# Revit family: K-Series Bar Joist-Rod Web
name_source: partatom
category: Structural Framing
revit_build: Autodesk Revit Architecture 2012 (Build: 20110210_1515)
units: mm (PartAtom-declared; Revit-internal decimal feet)

## types (64) — shared parameters
Assembly Code = B1010350
Chord Thickness = 0' - 0 1/4"
Cord Leg = 0' - 1 1/4"
Rendering Material = <By Category>
Seat Depth = 0' - 2 1/2"
Seat Length = 0' - 4"
Web Thickness = 0' - 0 3/8"

## per-type parameters (varying)
| type | Depth | End Panel | Wt |
| 8K1 | 0' - 8" | 1' - 4" | 5 |
| 10K1 | 0' - 10" | 1' - 8" | 5 |
| 12K1 | 1' - 0" | 2' - 0" | 5 |
| 12K3 | 1' - 0" | 2' - 0" | 6 |
| 12K5 | 1' - 0" | 2' - 0" | 7 |
| 14K1 | 1' - 2" | 2' - 4" | 5 |
| 14K3 | 1' - 2" | 2' - 4" | 6 |
| 14K4 | 1' - 2" | 2' - 4" | 7 |
| 14K6 | 1' - 2" | 2' - 4" | 8 |
| 16K2 | 1' - 4" | 2' - 8" | 6 |
| 16K3 | 1' - 4" | 2' - 8" | 6 |
| 16K4 | 1' - 4" | 2' - 8" | 7 |
| 16K5 | 1' - 4" | 2' - 8" | 8 |
| 16K6 | 1' - 4" | 2' - 8" | 8 |
| 16K7 | 1' - 4" | 2' - 8" | 9 |
| 16K9 | 1' - 4" | 2' - 8" | 10 |
| 18K3 | 1' - 6" | 3' - 0" | 7 |
| 18K4 | 1' - 6" | 3' - 0" | 7 |
| 18K5 | 1' - 6" | 3' - 0" | 8 |
| 18K6 | 1' - 6" | 3' - 0" | 9 |
| 18K7 | 1' - 6" | 3' - 0" | 9 |
| 18K9 | 1' - 6" | 3' - 0" | 10 |
| 18K10 | 1' - 6" | 3' - 0" | 12 |
| 20K3 | 1' - 8" | 3' - 4" | 7 |
| 20K4 | 1' - 8" | 3' - 4" | 8 |
| 20K5 | 1' - 8" | 3' - 4" | 8 |
| 20K6 | 1' - 8" | 3' - 4" | 9 |
| 20K7 | 1' - 8" | 3' - 4" | 9 |
| 20K9 | 1' - 8" | 3' - 4" | 11 |
| 20K10 | 1' - 8" | 3' - 4" | 12 |
| 22K4 | 1' - 10" | 3' - 8" | 8 |
| 22K5 | 1' - 10" | 3' - 8" | 9 |
| 22K6 | 1' - 10" | 3' - 8" | 9 |
| 22K7 | 1' - 10" | 3' - 8" | 10 |
| 22K9 | 1' - 10" | 3' - 8" | 11 |
| 22K10 | 1' - 10" | 3' - 8" | 13 |
| 22K11 | 1' - 10" | 3' - 8" | 14 |
| 24K4 | 2' - 0" | 4' - 0" | 8 |
| 24K5 | 2' - 0" | 4' - 0" | 9 |
| 24K6 | 2' - 0" | 4' - 0" | 10 |
| 24K7 | 2' - 0" | 4' - 0" | 10 |
| 24K8 | 2' - 0" | 4' - 0" | 12 |
| 24K9 | 2' - 0" | 4' - 0" | 12 |
| 24K10 | 2' - 0" | 4' - 0" | 13 |
| 24K12 | 2' - 0" | 4' - 0" | 16 |
| 26K5 | 2' - 2" | 4' - 4" | 10 |
| 26K6 | 2' - 2" | 4' - 4" | 11 |
| 26K7 | 2' - 2" | 4' - 4" | 11 |
| 26K8 | 2' - 2" | 4' - 4" | 12 |
| 26K9 | 2' - 2" | 4' - 4" | 12 |
| 26K10 | 2' - 2" | 4' - 4" | 14 |
| 26K12 | 2' - 2" | 4' - 4" | 17 |
| 28K6 | 2' - 4" | 4' - 8" | 11 |
| 28K7 | 2' - 4" | 4' - 8" | 12 |
| 28K8 | 2' - 4" | 4' - 8" | 13 |
| 28K9 | 2' - 4" | 4' - 8" | 13 |
| 28K10 | 2' - 4" | 4' - 8" | 14 |
| 28K12 | 2' - 4" | 4' - 8" | 17 |
| 30K7 | 2' - 6" | 5' - 0" | 12 |
| 30K8 | 2' - 6" | 5' - 0" | 13 |
| 30K9 | 2' - 6" | 5' - 0" | 13 |
| 30K10 | 2' - 6" | 5' - 0" | 15 |
| 30K11 | 2' - 6" | 5' - 0" | 16 |
| 30K12 | 2' - 6" | 5' - 0" | 18 |

## geometry (parser evidence)
native form markers: Sweep x3
no freeform markers — native parametric forms only
